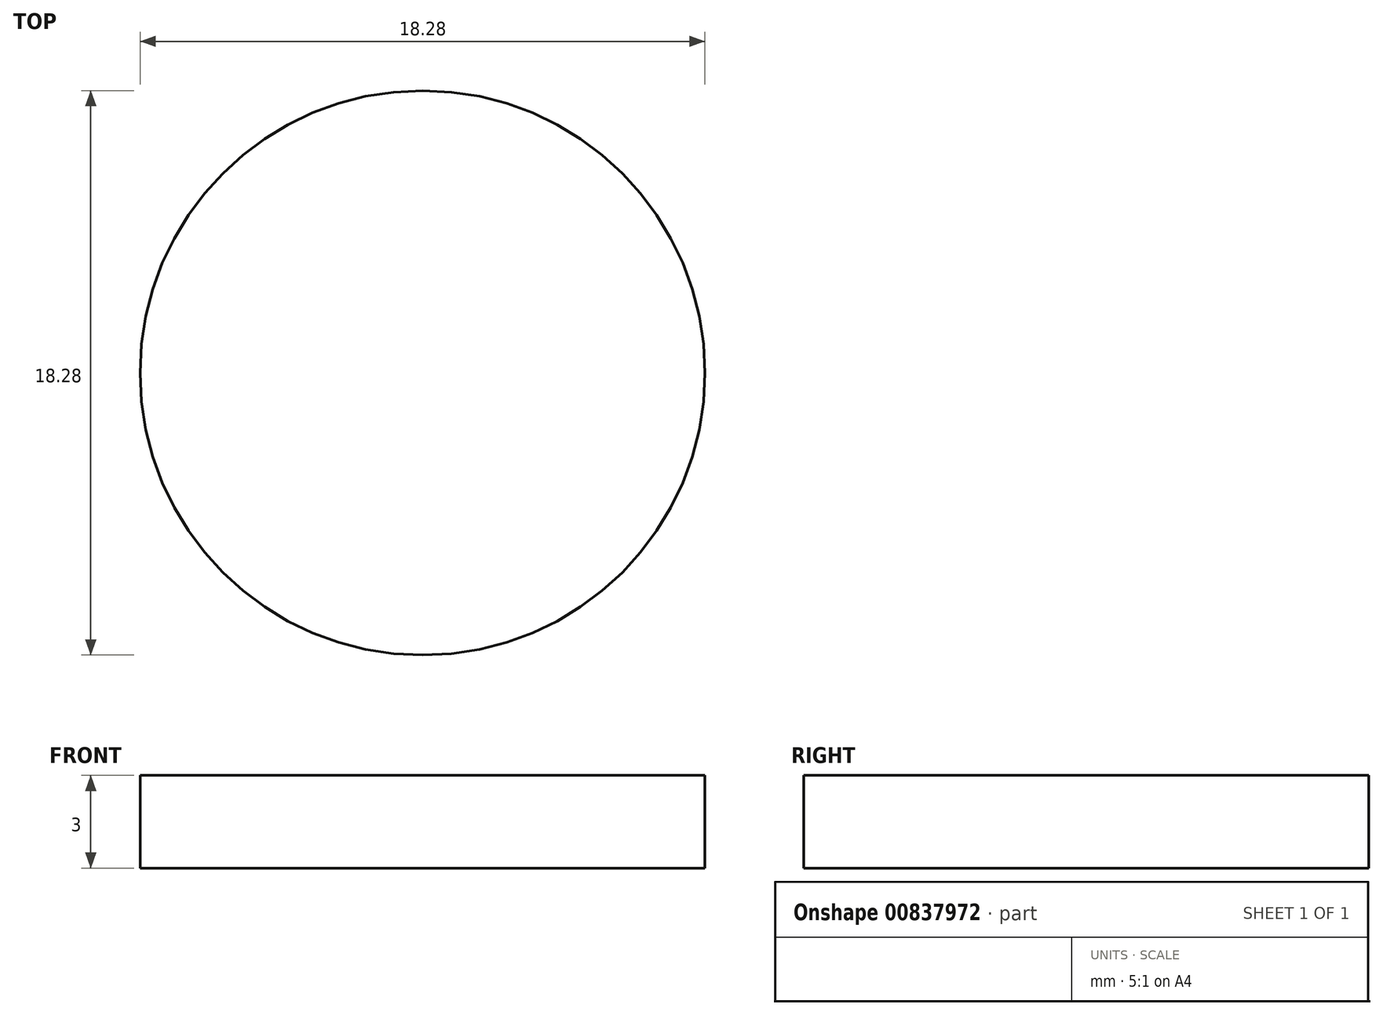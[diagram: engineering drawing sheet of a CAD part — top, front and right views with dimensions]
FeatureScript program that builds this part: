
annotation { "Feature Type Name" : "Feature", "Feature Type Description" : "" }
export const myFeature = defineFeature(function(context is Context, id is Id, definition is map)
    precondition{}
    {
        {
            var Q0;
            Q0=qCreatedBy(makeId("Top.planeOp"),FACE);
            var sketch = newSketch(context, id + "F0", { "sketchPlane" : qUnion([Q0])});
            skLineSegment(sketch, "E0.right", {"start": v(11, 1) * mm, "end": v(11, -1) * mm});
            skPoint(sketch, "E0.middle", {"position": v(0, 0) * mm});
            skPoint(sketch, "E1.visualSharp", {"position": v(-11, 2) * mm});
            skArc(sketch, "E1.filletArc", {"start": v(-10, 2) * mm, "mid": v(-10.7, 1.7) * mm, "end": v(-11, 1) * mm});
            skPoint(sketch, "E2.visualSharp", {"position": v(-11, -2) * mm});
            skArc(sketch, "E2.filletArc", {"start": v(-11, -1) * mm, "mid": v(-10.7, -1.7) * mm, "end": v(-10, -2) * mm});
            skPoint(sketch, "E3.visualSharp", {"position": v(11, 2) * mm});
            skArc(sketch, "E3.filletArc", {"start": v(11, 1) * mm, "mid": v(10.7, 1.7) * mm, "end": v(10, 2) * mm});
            skPoint(sketch, "E4.visualSharp", {"position": v(11, -2) * mm});
            skArc(sketch, "E4.filletArc", {"start": v(10, -2) * mm, "mid": v(10.7, -1.7) * mm, "end": v(11, -1) * mm});
            skArc(sketch, "E5.3", {"start": v(-14, -1) * mm, "mid": v(-12.83, -3.83) * mm, "end": v(-10, -5) * mm});
            skArc(sketch, "E5.4", {"start": v(14, 1) * mm, "mid": v(12.83, 3.83) * mm, "end": v(10, 5) * mm});
            skLineSegment(sketch, "E5.5", {"start": v(14, 1) * mm, "end": v(14, -1) * mm});
            skArc(sketch, "E5.6", {"start": v(10, -5) * mm, "mid": v(12.83, -3.83) * mm, "end": v(14, -1) * mm});
            skLineSegment(sketch, "E5.7", {"start": v(-10, -5) * mm, "end": v(10, -5) * mm});
            skCircle(sketch, "E6", {"center": v(0, 0) * mm, "radius": 9.14 * mm});
            skSolve(sketch);
        }
        {
            var Q0;
            Q0=qSketchRegion(id+"F0",true);
            extrude(context, id + "F1", {"entities" : qUnion([Q0]), "depth" : 3 * mm, "offsetDistance" : 25 * mm});
        }
    });
